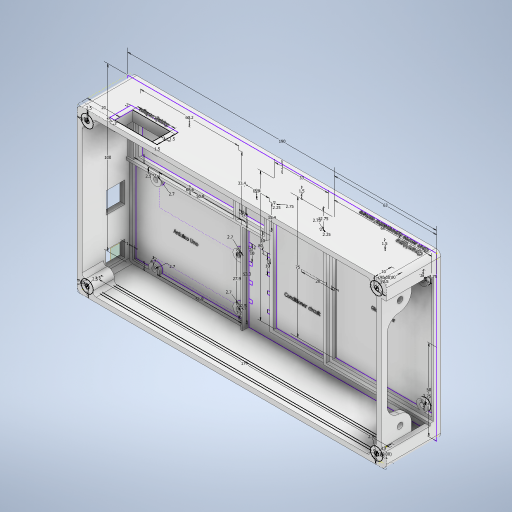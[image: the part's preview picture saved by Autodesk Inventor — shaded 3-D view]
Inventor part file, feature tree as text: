
AUTODESK INVENTOR PART (.ipt)
format: ipt  version: 2023 (Build 270158000, 158)  size: 3,770,368 bytes
history: native  units: mm
features: extrude x23, sketch x9, fillet x5, plane x2
ambient origin geometry x8: Origin, YZ Plane, XZ Plane, XY Plane, X Axis, Y Axis, Z Axis, Center Point
bodies: Body1 (feature_tree)
feature tree (39):
  sketch  "Sketch4"  dims[d12=2.0mm d20=1.5mm d24=2.0mm d25=1.5mm d34=1.0mm d41=1.5mm d97=63.0mm]
  extrude  "Extrusion6"  Depth=1.0mm
  extrude  "Extrusion7"  Depth=60.0mm
  extrude  "Extrusion9"  Depth=1.0mm
  extrude  "Extrusion10"  Depth=4.0mm
  extrude  "Extrusion15"  Depth=2.75mm
  extrude  "Extrusion16"  Depth=4.0mm
  extrude  "Extrusion17"  Depth=2.75mm
  extrude  "Extrusion18"  Depth=2.0mm TaperAngle=0.0deg
  extrude  "Extrusion19"  Depth=3.0mm
  extrude  "Extrusion20"  Depth=3.0mm
  extrude  "Extrusion21"  Depth=3.0mm
  sketch  "Sketch5"  dims[d98=75.0mm d99=60.0mm]
  sketch  "Sketch6"  dims[d100=1.0mm d101=1.0mm]
  extrude  "Extrusion22"  Depth=1.0mm
  extrude  "Extrusion23"  Depth=3.0mm
  extrude  "Extrusion24"  Depth=3.0mm
  sketch  "Sketch7"  dims[d102=1.5mm d105=4.0mm]
  sketch  "Sketch9"  dims[d106=4.0mm d107=2.75mm]
  extrude  "Extrusion34"  Depth=3.0mm
  extrude  "Extrusion35"  Depth=3.0mm
  fillet  "Fillet5"  Radius=2.75mm
  fillet  "Fillet7"  Radius=2.0mm
  sketch  "Sketch16"  dims[d110=4.0mm d111=2.75mm]
  extrude  "Extrusion38"  Depth=3.0mm
  extrude  "Extrusion39"  Depth=3.0mm
  extrude  "Extrusion40"  Depth=3.0mm
  fillet  "Fillet10"  Radius=2.0mm
  extrude  "Extrusion42"  Depth=3.0mm
  fillet  "Fillet11"  Radius=190.0mm
  plane  "Work Plane2"
  sketch  "Sketch21"  dims[d112=2.0mm d113=2.0mm d114=0.0mm]
  plane  "Work Plane3"
  sketch  "Sketch22"  dims[d115=4.0mm d116=0.0mm d117=20.0mm d118=33.0mm d119=80.0mm d120=1.0mm d121=2.0mm d122=1.5mm d123=2.25mm d124=12.75mm d125=2.75mm d126=2.0mm d127=2.25mm d128=2.75mm d129=2.0mm d132=2.0mm d133=0.0mm d134=50.0mm d135=190.0mm d136=100.0mm d137=3.0mm d138=31.0mm d139=0.0mm d140=1.0mm d141=1.0mm d142=68.6mm d143=53.3mm d144=1.0mm d145=1.0mm d146=1.5mm d151=2.5mm d152=7.2mm d153=51.9mm d154=4.7mm d155=27.9mm d156=50.8mm d158=2.7mm d159=2.0mm d163=2.5mm d166=2.7mm d167=2.0mm d168=2.7mm d169=2.0mm d174=1.0mm d175=60.2mm d176=33.4mm d177=1.0mm d178=1.0mm d179=1.5mm d184=2.5mm d185=0.0mm d186=1.0mm d187=2.7mm d188=2.0mm d190=17.4mm d191=1.0mm d192=1.0mm d193=15.4mm d194=15.4mm d195=1.0mm d196=1.0mm d197=1.5mm d198=4.0mm d199=0.0mm d200=3.0mm d201=0.0mm d202=2.0mm d203=0.0mm d204=2.0mm d205=0.0mm d206=4.0mm d207=0.0mm d208=2.0mm d209=0.0mm d210=2.0mm d211=1.7mm d212=16.4mm d213=11.7mm d214=9.8mm d215=48.0mm d216=11.5mm d217=13.0mm d218=20.0mm d219=3.0mm d220=23.0mm d221=11.0mm d223=3.0mm d224=3.0mm d225=0.0mm d226=2.0mm d227=3.0mm d228=6.3mm d229=0.0mm d230=3.0mm d231=0.0mm d232=3.0mm d233=1.5mm d234=10.0mm d235=1.5mm d236=5.0mm d237=10.0mm d238=90.0deg d256=5.0mm d257=3.0mm d258=1.5mm d259=10.0mm d260=90.0deg d261=179.0mm d262=1.5mm d298=10.0mm d299=2.0mm d300=2.0mm d301=40.0mm d303=10.0mm d304=10.0mm d306=10.0mm d308=2.0mm d309=2.0mm d310=40.0mm d312=10.0mm d313=10.0mm d315=10.0mm d326=0.25mm d327=0.0mm d328=3.5mm d329=15.0mm d330=20.0mm d331=15.0mm d332=20.0mm d333=13.5mm d334=8.0mm d335=3.5mm d336=13.5mm d337=8.0mm d338=90.0deg d339=3.5mm d340=3.0mm d341=0.0mm d342=8.0mm d348=2.0mm d349=6.0mm d350=6.0mm d351=2.5mm d352=2.5mm d353=6.0mm d354=6.0mm d355=2.5mm d356=2.5mm d357=6.0mm d358=6.0mm d359=2.5mm d360=2.5mm d361=6.0mm d362=6.0mm d363=2.5mm d364=2.5mm d365=3.0mm d366=0.0mm d367=12.0mm d368=0.0mm d369=13.0mm d370=0.0mm d375=2.0mm d376=0.0mm d377=28.0mm d378=180.0deg d379=17.0mm d382=2.0mm d383=0.25mm d384=0.0mm d385=1.0mm d390=0.5mm d391=0.0mm d392=0.5mm d393=0.0mm d394=3.0mm d395=0.0mm d396=3.0mm d21=0.5mm d22=0.872665mm d23=0.5mm d239=0.5mm d240=0.872665mm d241=0.5mm d242=0.872665mm d243=0.5mm d244=0.872665mm d245=0.5mm d246=0.872665mm d311=0.872665mm d319=0.5mm d320=0.872665mm d321=0.5mm d322=0.872665mm d371=0.5mm d372=0.872665mm d373=0.5mm d374=0.872665mm]
  extrude  "Extrusion45"  Depth=100.0mm
  extrude  "Extrusion46"  Depth=3.0mm
  extrude  "Extrusion47"  Depth=3.0mm TaperAngle=0.0deg
  fillet  "Fillet12"  Radius=1.0mm
  sketch  "Sketch15"  dims[d108=2.0mm d109=4.0mm]
